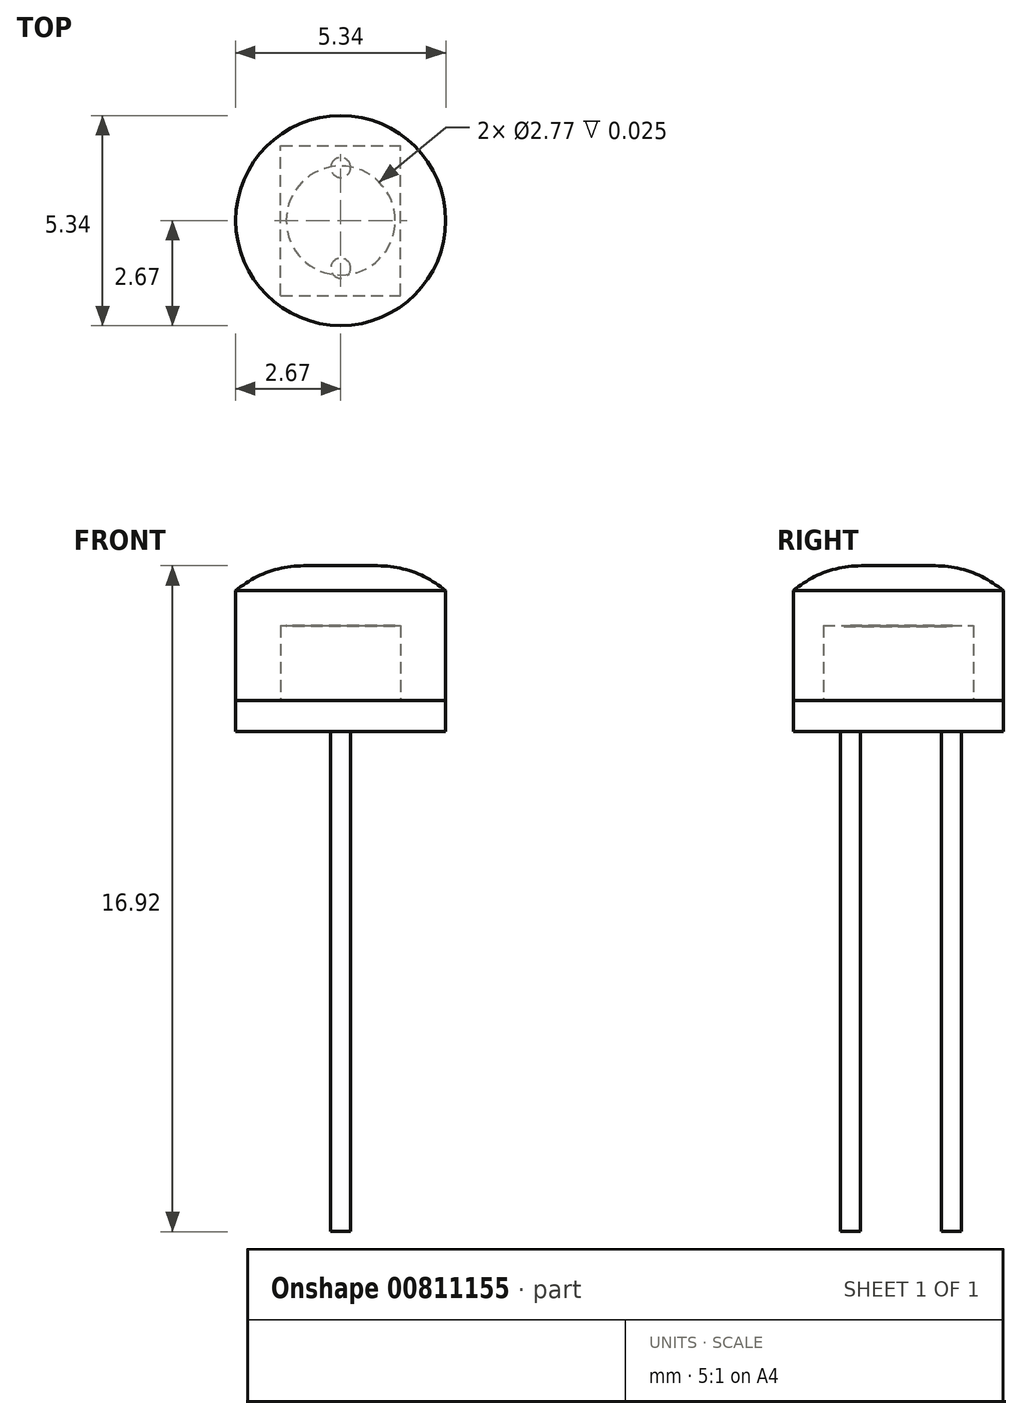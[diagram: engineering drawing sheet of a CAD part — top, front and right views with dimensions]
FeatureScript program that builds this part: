
annotation { "Feature Type Name" : "Feature", "Feature Type Description" : "" }
export const myFeature = defineFeature(function(context is Context, id is Id, definition is map)
    precondition{}
    {
        {
            var Q0;
            Q0=qCreatedBy(makeId("Top.planeOp"),FACE);
            var sketch = newSketch(context, id + "F0", { "sketchPlane" : qUnion([Q0])});
            skCircle(sketch, "E0", {"center": v(0, 0) * mm, "radius": 2.67 * mm});
            skSolve(sketch);
        }
        {
            var Q0;
            Q0 = qSketchRegion(id + "F0", true);
            extrude(context, id + "F1", {"entities" : qUnion([Q0]), "oppositeDirection" : true, "depth" : 0.79 * mm, "offsetDistance" : 25.4 * mm});
        }
        {
            var Q0;
            Q0=makeQuery(id+"F1.opExtrude","CAP_FACE",FACE,{"disambiguationData":[OSD([sQuery(id+"F0.wireOp",EDGE,"E0")])],"isStart":true});
            var sketch = newSketch(context, id + "F2", { "sketchPlane" : qUnion([Q0])});
            skLineSegment(sketch, "E1.bottom", {"start": v(-1.52, -1.9) * mm, "end": v(1.52, -1.9) * mm});
            skLineSegment(sketch, "E1.top", {"start": v(-1.52, 1.9) * mm, "end": v(1.52, 1.9) * mm});
            skLineSegment(sketch, "E1.left", {"start": v(-1.52, -1.9) * mm, "end": v(-1.52, 1.9) * mm});
            skLineSegment(sketch, "E1.right", {"start": v(1.52, -1.9) * mm, "end": v(1.52, 1.9) * mm});
            skPoint(sketch, "E1.middle", {"position": v(0, 0) * mm});
            skSolve(sketch);
        }
        {
            var Q0;
            Q0 = qSketchRegion(id + "F2", true);
            extrude(context, id + "F3", {"entities" : qUnion([Q0]), "depth" : 1.9 * mm, "offsetDistance" : 25.4 * mm});
        }
        {
            var Q0;
            Q0=makeQuery(id+"F1.opExtrude","CAP_FACE",FACE,{"disambiguationData":[OSD([sQuery(id+"F0.wireOp",EDGE,"E0")])],"isStart":true});
            extrude(context, id + "F4", {"entities" : qUnion([Q0]), "depth" : 2.8 * mm, "offsetDistance" : 25.4 * mm});
        }
        {
            var Q0;
            Q0=makeQuery(id+"F3.opExtrude","CAP_FACE",FACE,{"disambiguationData":[OSD([sQuery(id+"F2.wireOp",EDGE,"E1.bottom"),sQuery(id+"F2.wireOp",EDGE,"E1.top"),sQuery(id+"F2.wireOp",EDGE,"E1.left"),sQuery(id+"F2.wireOp",EDGE,"E1.right")])],"isStart":false});
            var sketch = newSketch(context, id + "F5", { "sketchPlane" : qUnion([Q0])});
            skCircle(sketch, "E2", {"center": v(0, 0) * mm, "radius": 1.38 * mm});
            skSolve(sketch);
        }
        {
            var Q0;
            Q0 = qSketchRegion(id + "F5", true);
            extrude(context, id + "F6", {"entities" : qUnion([Q0]), "operationType" : NewBodyOperationType.REMOVE, "oppositeDirection" : true, "depth" : 0.03 * mm, "offsetDistance" : 25.4 * mm});
        }
        {
            var Q0;
            Q0=makeQuery(id+"F4.opExtrude","CAP_FACE",FACE,{"disambiguationData":[OSD([sQuery(id+"F0.wireOp",EDGE,"E0")])],"isStart":false});
            extrude(context, id + "F7", {"entities" : qUnion([Q0]), "depth" : 0.64 * mm, "offsetDistance" : 25.4 * mm});
        }
        {
            var Q0;
            Q0=makeQuery(id+"F7.opExtrude","CAP_EDGE",EDGE,{"disambiguationData":[OSD([sQuery(id+"F0.wireOp",EDGE,"E0")])],"isStart":false});
            fillet(context, id + "F8", {"entities" : qUnion([Q0]), "radius" : 2.67 * mm, "tangentPropagation" : true, "allowEdgeOverflow" : false});
        }
        {
            var Q0;
            Q0=makeQuery(id+"F1.opExtrude","CAP_FACE",FACE,{"disambiguationData":[OSD([sQuery(id+"F0.wireOp",EDGE,"E0")])],"isStart":false});
            var sketch = newSketch(context, id + "F9", { "sketchPlane" : qUnion([Q0])});
            skCircle(sketch, "E3", {"center": v(0, 1.2) * mm, "radius": 0.25 * mm});
            skCircle(sketch, "E4", {"center": v(0, -1.35) * mm, "radius": 0.25 * mm});
            skSolve(sketch);
        }
        {
            var Q0;
            Q0 = qSketchRegion(id + "F9", true);
            extrude(context, id + "F10", {"entities" : qUnion([Q0]), "depth" : 12.7 * mm, "offsetDistance" : 25.4 * mm});
        }
    });
